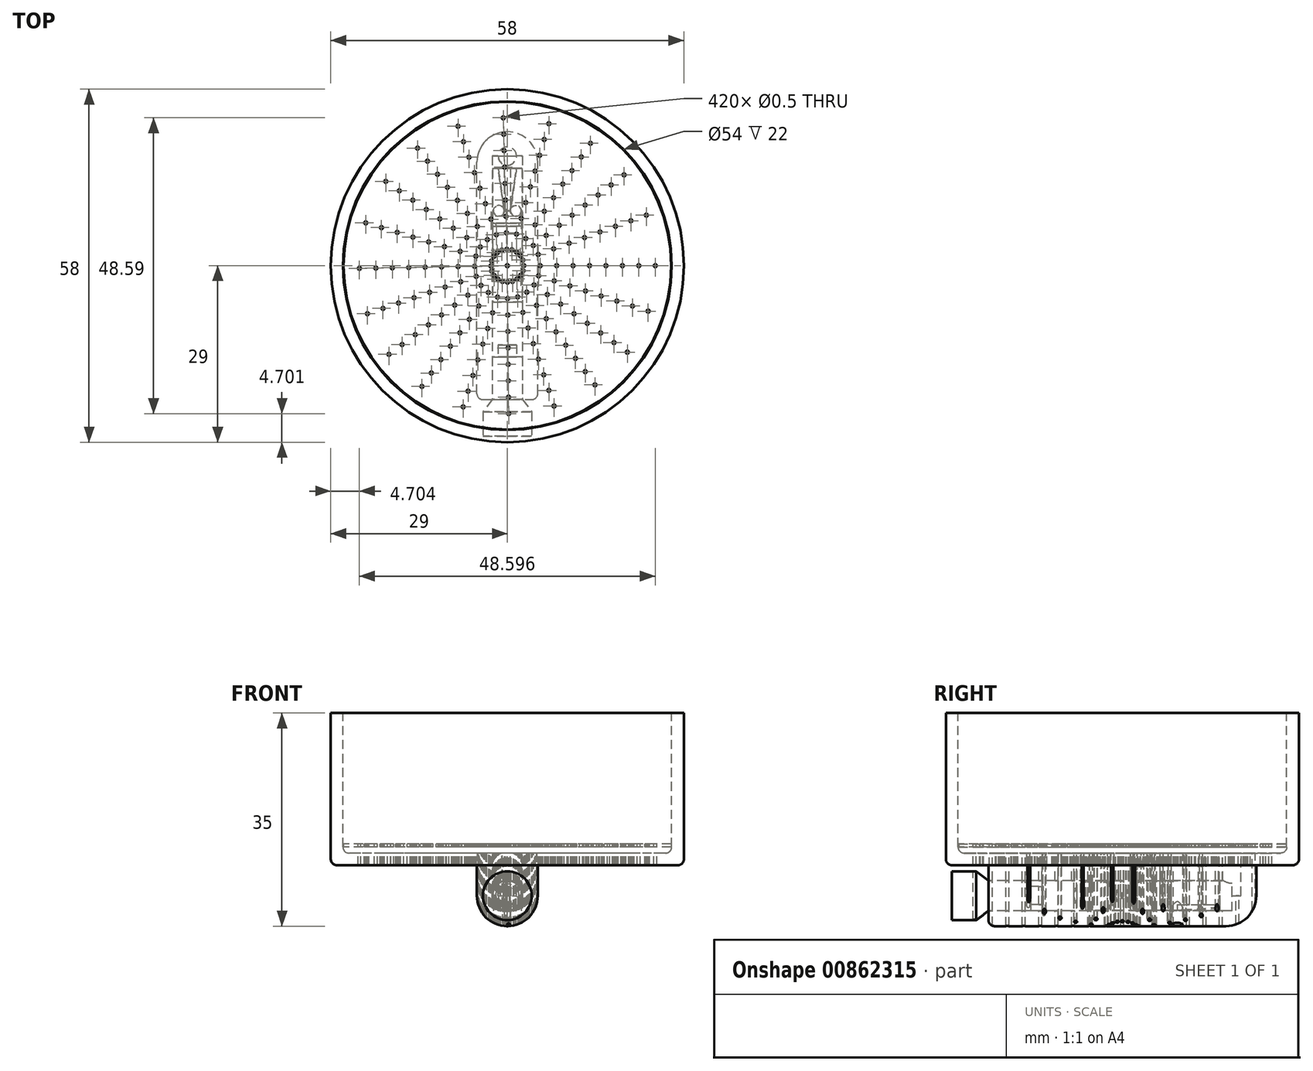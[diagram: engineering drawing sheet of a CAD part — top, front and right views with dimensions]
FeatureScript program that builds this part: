
annotation { "Feature Type Name" : "Feature", "Feature Type Description" : "" }
export const myFeature = defineFeature(function(context is Context, id is Id, definition is map)
    precondition{}
    {
        {
            var Q0;
            Q0=qCreatedBy(makeId("Top.planeOp"),FACE);
            var sketch = newSketch(context, id + "F0", { "sketchPlane" : qUnion([Q0])});
            skCircle(sketch, "E0", {"center": v(0, 0) * mm, "radius": 29 * mm});
            skSolve(sketch);
        }
        {
            var Q0;
            Q0=makeQuery(id+"F0.imprint","IMPRINT",FACE,{"disambiguationData":[TD([[makeQuery(id+"F0.imprint","IMPRINT",EDGE,{"derivedFrom":sQuery(id+"F0.wireOp",EDGE,"E0")}),1.0]])]});
            extrude(context, id + "F1", {"entities" : qUnion([Q0]), "oppositeDirection" : true, "depth" : 25 * mm, "offsetDistance" : 25 * mm});
        }
        {
            var Q0;
            Q0=makeQuery(id+"F1.opExtrude","CAP_FACE",FACE,{"disambiguationData":[OSD([sQuery(id+"F0.wireOp",EDGE,"E0")])],"isStart":true});
            shell(context, id + "F2", {"entities" : qUnion([Q0]), "thickness" : 2 * mm});
        }
        {
            var Q0;
            Q0=qCreatedBy(makeId("Front.planeOp"),FACE);
            var sketch = newSketch(context, id + "F3", { "sketchPlane" : qUnion([Q0])});
            skLineSegment(sketch, "E1.bottom", {"start": v(-5, -25) * mm, "end": v(5, -25) * mm});
            skLineSegment(sketch, "E1.top", {"start": v(-5, -35) * mm, "end": v(5, -35) * mm});
            skLineSegment(sketch, "E1.left", {"start": v(-5, -25) * mm, "end": v(-5, -35) * mm});
            skLineSegment(sketch, "E1.right", {"start": v(5, -25) * mm, "end": v(5, -35) * mm});
            skLineSegment(sketch, "E2.0", {"start": v(-29, -25) * mm, "end": v(29, -25) * mm});
            skSolve(sketch);
        }
        {
            var Q0;
            Q0=makeQuery(id+"F3.imprint","IMPRINT",FACE,{"disambiguationData":[TD([[makeQuery(id+"F3.imprint","IMPRINT",EDGE,{"derivedFrom":sQuery(id+"F3.wireOp",EDGE,"E1.top")}),1.0]])]});
            extrude(context, id + "F4", {"entities" : qUnion([Q0]), "operationType" : NewBodyOperationType.ADD, "depth" : 22 * mm, "offsetDistance" : 25 * mm, "hasSecondDirection" : true, "secondDirectionOppositeDirection" : true, "secondDirectionDepth" : 22 * mm});
        }
        {
            var Q0;
            Q0=makeQuery(id+"F4.opExtrude","CAP_FACE",FACE,{"disambiguationData":[OSD([sQuery(id+"F3.wireOp",EDGE,"E1.top"),sQuery(id+"F3.wireOp",EDGE,"E1.left"),sQuery(id+"F3.wireOp",EDGE,"E1.right"),sQuery(id+"F3.wireOp",EDGE,"E2.0")])],"isStart":false});
            var sketch = newSketch(context, id + "F5", { "sketchPlane" : qUnion([Q0])});
            skCircle(sketch, "E3", {"center": v(0, -30) * mm, "radius": 2.5 * mm});
            skLineSegment(sketch, "E4", {"start": v(-7.7, -30) * mm, "end": v(7.12, -30) * mm, "construction": true});
            skPoint(sketch, "E5", {"position": v(0, -32.45) * mm});
            skSolve(sketch);
        }
        {
            var Q0;
            Q0=makeQuery(id+"F5.imprint","IMPRINT",FACE,{"disambiguationData":[TD([[makeQuery(id+"F5.imprint","IMPRINT",EDGE,{"derivedFrom":sQuery(id+"F5.wireOp",EDGE,"E3")}),1.0]])]});
            extrude(context, id + "F6", {"entities" : qUnion([Q0]), "operationType" : NewBodyOperationType.REMOVE, "oppositeDirection" : true, "depth" : 40 * mm, "offsetDistance" : 25 * mm});
        }
        {
            var Q0;
            Q0=makeQuery(id+"F5.imprint","IMPRINT",FACE,{"disambiguationData":[TD([[makeQuery(id+"F5.imprint","IMPRINT",EDGE,{"derivedFrom":sQuery(id+"F5.wireOp",EDGE,"E3")}),-1.0]])]});
            cPlane(context, id + "F7", {"entities" : qUnion([Q0]), "cplaneType" : CPlaneType.OFFSET, "offset" : 20 * mm, "oppositeDirection" : true, "width" : 150 * mm, "height" : 150 * mm});
        }
        {
            var Q0;
            Q0=qCreatedBy(id+"F7.planeOp",FACE);
            var sketch = newSketch(context, id + "F8", { "sketchPlane" : qUnion([Q0])});
            skCircle(sketch, "E6", {"center": v(0, -30) * mm, "radius": 2.43 * mm});
            skSolve(sketch);
        }
        {
            var Q0;
            Q0=makeQuery(id+"F8.imprint","IMPRINT",FACE,{"disambiguationData":[TD([[makeQuery(id+"F8.imprint","IMPRINT",EDGE,{"derivedFrom":sQuery(id+"F8.wireOp",EDGE,"E6")}),1.0]])]});
            extrude(context, id + "F9", {"entities" : qUnion([Q0]), "oppositeDirection" : true, "depth" : 18 * mm, "offsetDistance" : 25 * mm, "hasSecondDirection" : true, "secondDirectionOppositeDirection" : false, "secondDirectionDepth" : 4 * mm});
        }
        {
            var Q0;
            Q0=sQuery(id+"F5.wireOp",VERTEX,"E5");
            var Q1;
            Q1=qCreatedBy(makeId("Top.planeOp"),FACE);
            cPlane(context, id + "F10", {"entities" : qUnion([Q0, Q1]), "cplaneType" : CPlaneType.PLANE_POINT, "offset" : 25 * mm, "width" : 150 * mm, "height" : 150 * mm});
        }
        {
            var Q0;
            Q0=qCreatedBy(id+"F10.planeOp",FACE);
            var sketch = newSketch(context, id + "F11", { "sketchPlane" : qUnion([Q0])});
            skLineSegment(sketch, "E7", {"start": v(-0.5, 9) * mm, "end": v(0.5, 9) * mm});
            skLineSegment(sketch, "E8", {"start": v(0.5, 9) * mm, "end": v(1.5, 16) * mm});
            skLineSegment(sketch, "E9", {"start": v(-0.5, 9) * mm, "end": v(-1.5, 16) * mm});
            skLineSegment(sketch, "E10", {"start": v(-1.5, 16) * mm, "end": v(1.5, 16) * mm});
            skLineSegment(sketch, "E11", {"start": v(0, -13.78) * mm, "end": v(0, 12.24) * mm, "construction": true});
            skLineSegment(sketch, "E12.0", {"start": v(2.43, 16) * mm, "end": v(-2.43, 16) * mm, "construction": true});
            skSolve(sketch);
        }
        {
            var Q0;
            Q0=makeQuery(id+"F11.imprint","IMPRINT",FACE,{"disambiguationData":[TD([[makeQuery(id+"F11.imprint","IMPRINT",EDGE,{"derivedFrom":sQuery(id+"F11.wireOp",EDGE,"E8")}),1.0]])]});
            extrude(context, id + "F12", {"entities" : qUnion([Q0]), "operationType" : NewBodyOperationType.REMOVE, "depth" : 1 * mm, "offsetDistance" : 25 * mm});
        }
        {
            var Q0;
            Q0=sQuery(id+"F5.wireOp",VERTEX,"E3.center");
            var Q1;
            Q1=qCreatedBy(makeId("Top.planeOp"),FACE);
            cPlane(context, id + "F13", {"entities" : qUnion([Q0, Q1]), "cplaneType" : CPlaneType.PLANE_POINT, "offset" : 25 * mm, "width" : 150 * mm, "height" : 150 * mm});
        }
        {
            var Q0;
            Q0=qCreatedBy(id+"F13.planeOp",FACE);
            var sketch = newSketch(context, id + "F14", { "sketchPlane" : qUnion([Q0])});
            skLineSegment(sketch, "E13.0", {"start": v(2.43, -6) * mm, "end": v(-2.43, -6) * mm, "construction": true});
            skLineSegment(sketch, "E14.bottom", {"start": v(1.92, 6.5) * mm, "end": v(2.42, 6.5) * mm});
            skLineSegment(sketch, "E14.top", {"start": v(1.92, 7) * mm, "end": v(2.42, 7) * mm});
            skLineSegment(sketch, "E14.left", {"start": v(1.92, 6.5) * mm, "end": v(1.92, 7) * mm});
            skLineSegment(sketch, "E14.right", {"start": v(2.42, 6.5) * mm, "end": v(2.42, 7) * mm});
            skLineSegment(sketch, "E15", {"start": v(0, 0) * mm, "end": v(0, -5.82) * mm, "construction": true});
            skPoint(sketch, "E15.endSnap0", {"position": v(0, -6) * mm});
            skSolve(sketch);
        }
        {
            var Q0;
            Q0=makeQuery(id+"F14.imprint","IMPRINT",FACE,{"disambiguationData":[TD([[makeQuery(id+"F14.imprint","IMPRINT",EDGE,{"derivedFrom":sQuery(id+"F14.wireOp",EDGE,"E14.bottom")}),1.0]])]});
            var Q1;
            Q1=sQuery(id+"F14.wireOp",EDGE,"E15");
            revolve(context, id + "F15", {"operationType" : NewBodyOperationType.REMOVE, "surfaceOperationType" : NewSurfaceOperationType.NEW, "entities" : qUnion([Q0]), "axis" : qUnion([Q1]), "revolveType" : RevolveType.FULL, "oppositeDirection" : true});
        }
        {
            var Q0;
            Q0=makeQuery(id+"F4.opExtrude","SWEPT_FACE",FACE,{"disambiguationData":[OSD([sQuery(id+"F3.wireOp",EDGE,"E1.top")])]});
            var sketch = newSketch(context, id + "F16", { "sketchPlane" : qUnion([Q0])});
            skCircle(sketch, "E16", {"center": v(1.4, -9) * mm, "radius": 0.9 * mm});
            skCircle(sketch, "E17", {"center": v(-1.4, -9) * mm, "radius": 0.9 * mm});
            skSolve(sketch);
        }
        {
            var Q0;
            Q0=makeQuery(id+"F16.imprint","IMPRINT",FACE,{"disambiguationData":[TD([[makeQuery(id+"F16.imprint","IMPRINT",EDGE,{"derivedFrom":sQuery(id+"F16.wireOp",EDGE,"E17")}),1.0]])]});
            var Q1;
            Q1=makeQuery(id+"F16.imprint","IMPRINT",FACE,{"disambiguationData":[TD([[makeQuery(id+"F16.imprint","IMPRINT",EDGE,{"derivedFrom":sQuery(id+"F16.wireOp",EDGE,"E16")}),1.0]])]});
            var Q2;
            Q2=makeQuery(id+"F9.opExtrude","SWEPT_BODY",BODY,{"disambiguationData":[OSD([sQuery(id+"F8.wireOp",EDGE,"E6")])]});
            extrude(context, id + "F17", {"entities" : qUnion([Q0, Q1]), "operationType" : NewBodyOperationType.REMOVE, "endBound" : BoundingType.UP_TO_NEXT, "oppositeDirection" : true, "depth" : 25 * mm, "endBoundEntityBody" : qUnion([Q2]), "offsetDistance" : 25 * mm});
        }
        {
            var Q0;
            {var subQ0=sQuery(id+"F0.wireOp",EDGE,"E0");Q0=makeQuery(id+"F2.opShell","OFFSET_FACE",FACE,{"disambiguationData":[OSD([subQ0]),TDD([makeQuery(id+"F1.opExtrude","CAP_FACE",FACE,{"disambiguationData":[OSD([subQ0])],"isStart":false})])]});}
            var sketch = newSketch(context, id + "F18", { "sketchPlane" : qUnion([Q0])});
            skCircle(sketch, "E18", {"center": v(0, 18) * mm, "radius": 1.5 * mm});
            skCircle(sketch, "E19.0.0", {"center": v(0, 0) * mm, "radius": 29 * mm});
            skPoint(sketch, "E20.0", {"position": v(0, 16) * mm});
            skPoint(sketch, "E21", {"position": v(0, 19.5) * mm});
            skSolve(sketch);
        }
        {
            var Q0;
            Q0=makeQuery(id+"F18.imprint","IMPRINT",FACE,{"disambiguationData":[TD([[makeQuery(id+"F18.imprint","IMPRINT",EDGE,{"derivedFrom":sQuery(id+"F18.wireOp",EDGE,"E18")}),1.0]])]});
            var Q1;
            Q1=sQuery(id+"F5.wireOp",VERTEX,"E3.center");
            extrude(context, id + "F19", {"entities" : qUnion([Q0]), "operationType" : NewBodyOperationType.REMOVE, "endBound" : BoundingType.UP_TO_VERTEX, "oppositeDirection" : true, "depth" : 25 * mm, "endBoundEntityVertex" : qUnion([Q1]), "offsetDistance" : 25 * mm});
        }
        {
            var Q0;
            Q0=qCreatedBy(id+"F13.planeOp",FACE);
            var sketch = newSketch(context, id + "F20", { "sketchPlane" : qUnion([Q0])});
            skLineSegment(sketch, "E22.0", {"start": v(2.5, -22) * mm, "end": v(-2.5, -22) * mm, "construction": true});
            skLineSegment(sketch, "E23", {"start": v(2.5, -22) * mm, "end": v(4, -24) * mm});
            skLineSegment(sketch, "E24", {"start": v(0, -27) * mm, "end": v(0, -13) * mm});
            skPoint(sketch, "E24.endSnap0", {"position": v(0, -22) * mm});
            skLineSegment(sketch, "E25", {"start": v(0, -13) * mm, "end": v(1.5, -13) * mm});
            skLineSegment(sketch, "E26", {"start": v(1.5, -13) * mm, "end": v(1.5, -15) * mm});
            skLineSegment(sketch, "E27", {"start": v(1.5, -15) * mm, "end": v(2.5, -15) * mm});
            skLineSegment(sketch, "E28", {"start": v(2.5, -15) * mm, "end": v(2.5, -22) * mm});
            skLineSegment(sketch, "E29", {"start": v(0, -27) * mm, "end": v(0, -28) * mm});
            skLineSegment(sketch, "E30", {"start": v(0, -28) * mm, "end": v(4, -28) * mm});
            skLineSegment(sketch, "E31", {"start": v(4, -28) * mm, "end": v(4, -24) * mm});
            skSolve(sketch);
        }
        {
            var Q0;
            Q0=makeQuery(id+"F20.imprint","IMPRINT",FACE,{"disambiguationData":[TD([[makeQuery(id+"F20.imprint","IMPRINT",EDGE,{"derivedFrom":sQuery(id+"F20.wireOp",EDGE,"E23")}),-1.0]])]});
            var Q1;
            Q1=sQuery(id+"F20.wireOp",EDGE,"E24");
            revolve(context, id + "F21", {"surfaceOperationType" : NewSurfaceOperationType.NEW, "entities" : qUnion([Q0]), "axis" : qUnion([Q1]), "revolveType" : RevolveType.FULL});
        }
        {
            var Q0;
            {var subQ0=sQuery(id+"F0.wireOp",EDGE,"E0");Q0=makeQuery(id+"F2.opShell","OFFSET_FACE",FACE,{"disambiguationData":[OSD([subQ0]),TDD([makeQuery(id+"F1.opExtrude","CAP_FACE",FACE,{"disambiguationData":[OSD([subQ0])],"isStart":false})])]});}
            cPlane(context, id + "F22", {"entities" : qUnion([Q0]), "cplaneType" : CPlaneType.OFFSET, "offset" : 1 * mm, "width" : 150 * mm, "height" : 150 * mm});
        }
        {
            var Q0;
            Q0=qCreatedBy(id+"F22.planeOp",FACE);
            var sketch = newSketch(context, id + "F23", { "sketchPlane" : qUnion([Q0])});
            skCircle(sketch, "E32", {"center": v(0, 0) * mm, "radius": 26.9 * mm});
            skSolve(sketch);
        }
        {
            var Q0;
            Q0=makeQuery(id+"F23.imprint","IMPRINT",FACE,{"disambiguationData":[TD([[makeQuery(id+"F23.imprint","IMPRINT",EDGE,{"derivedFrom":sQuery(id+"F23.wireOp",EDGE,"E32")}),1.0]])]});
            extrude(context, id + "F24", {"entities" : qUnion([Q0]), "depth" : 0.5 * mm, "offsetDistance" : 25 * mm});
        }
        {
            var Q0;
            Q0=makeQuery(id+"F24.opExtrude","CAP_FACE",FACE,{"disambiguationData":[OSD([sQuery(id+"F23.wireOp",EDGE,"E32")])],"isStart":false});
            var sketch = newSketch(context, id + "F25", { "sketchPlane" : qUnion([Q0])});
            skCircle(sketch, "E33", {"center": v(0, 0) * mm, "radius": 0.25 * mm});
            skCircle(sketch, "E34.1.0.0", {"center": v(2.7, 0) * mm, "radius": 0.25 * mm});
            skCircle(sketch, "E34.2.0.0", {"center": v(5.4, 0) * mm, "radius": 0.25 * mm});
            skCircle(sketch, "E34.3.0.0", {"center": v(8.1, 0) * mm, "radius": 0.25 * mm});
            skCircle(sketch, "E34.4.0.0", {"center": v(10.8, 0) * mm, "radius": 0.25 * mm});
            skCircle(sketch, "E34.5.0.0", {"center": v(13.5, 0) * mm, "radius": 0.25 * mm});
            skCircle(sketch, "E34.6.0.0", {"center": v(16.2, 0) * mm, "radius": 0.25 * mm});
            skCircle(sketch, "E34.7.0.0", {"center": v(18.9, 0) * mm, "radius": 0.25 * mm});
            skCircle(sketch, "E34.8.0.0", {"center": v(21.6, 0) * mm, "radius": 0.25 * mm});
            skCircle(sketch, "E34.9.0.0", {"center": v(24.3, 0) * mm, "radius": 0.25 * mm});
            skLineSegment(sketch, "E34.direction1", {"start": v(0, 0) * mm, "end": v(2.7, 0) * mm, "construction": true});
            skLineSegment(sketch, "E35.1.0", {"start": v(0, 0) * mm, "end": v(2.57, -0.83) * mm, "construction": true});
            skCircle(sketch, "E35.1.1", {"center": v(15.42, -4.98) * mm, "radius": 0.25 * mm});
            skCircle(sketch, "E35.1.2", {"center": v(10.28, -3.32) * mm, "radius": 0.25 * mm});
            skCircle(sketch, "E35.1.3", {"center": v(12.85, -4.15) * mm, "radius": 0.25 * mm});
            skCircle(sketch, "E35.1.4", {"center": v(7.7, -2.49) * mm, "radius": 0.25 * mm});
            skCircle(sketch, "E35.1.5", {"center": v(23.12, -7.47) * mm, "radius": 0.25 * mm});
            skCircle(sketch, "E35.1.6", {"center": v(20.56, -6.64) * mm, "radius": 0.25 * mm});
            skCircle(sketch, "E35.1.7", {"center": v(17.99, -5.8) * mm, "radius": 0.25 * mm});
            skCircle(sketch, "E35.1.8", {"center": v(5.14, -1.66) * mm, "radius": 0.25 * mm});
            skCircle(sketch, "E35.1.9", {"center": v(2.57, -0.83) * mm, "radius": 0.25 * mm});
            skLineSegment(sketch, "E35.2.0", {"start": v(0, 0) * mm, "end": v(2.2, -1.58) * mm, "construction": true});
            skCircle(sketch, "E35.2.1", {"center": v(13.14, -9.47) * mm, "radius": 0.25 * mm});
            skCircle(sketch, "E35.2.2", {"center": v(8.76, -6.32) * mm, "radius": 0.25 * mm});
            skCircle(sketch, "E35.2.3", {"center": v(10.95, -7.9) * mm, "radius": 0.25 * mm});
            skCircle(sketch, "E35.2.4", {"center": v(6.57, -4.74) * mm, "radius": 0.25 * mm});
            skCircle(sketch, "E35.2.5", {"center": v(19.71, -14.21) * mm, "radius": 0.25 * mm});
            skCircle(sketch, "E35.2.6", {"center": v(17.52, -12.63) * mm, "radius": 0.25 * mm});
            skCircle(sketch, "E35.2.7", {"center": v(15.33, -11.05) * mm, "radius": 0.25 * mm});
            skCircle(sketch, "E35.2.8", {"center": v(4.38, -3.16) * mm, "radius": 0.25 * mm});
            skCircle(sketch, "E35.2.9", {"center": v(2.2, -1.58) * mm, "radius": 0.25 * mm});
            skLineSegment(sketch, "E35.3.0", {"start": v(0, 0) * mm, "end": v(1.6, -2.18) * mm, "construction": true});
            skCircle(sketch, "E35.3.1", {"center": v(9.6, -13.05) * mm, "radius": 0.25 * mm});
            skCircle(sketch, "E35.3.2", {"center": v(6.4, -8.7) * mm, "radius": 0.25 * mm});
            skCircle(sketch, "E35.3.3", {"center": v(8, -10.88) * mm, "radius": 0.25 * mm});
            skCircle(sketch, "E35.3.4", {"center": v(4.8, -6.53) * mm, "radius": 0.25 * mm});
            skCircle(sketch, "E35.3.5", {"center": v(14.4, -19.58) * mm, "radius": 0.25 * mm});
            skCircle(sketch, "E35.3.6", {"center": v(12.8, -17.4) * mm, "radius": 0.25 * mm});
            skCircle(sketch, "E35.3.7", {"center": v(11.2, -15.23) * mm, "radius": 0.25 * mm});
            skCircle(sketch, "E35.3.8", {"center": v(3.2, -4.35) * mm, "radius": 0.25 * mm});
            skCircle(sketch, "E35.3.9", {"center": v(1.6, -2.18) * mm, "radius": 0.25 * mm});
            skLineSegment(sketch, "E35.4.0", {"start": v(0, 0) * mm, "end": v(0.85, -2.56) * mm, "construction": true});
            skCircle(sketch, "E35.4.1", {"center": v(5.12, -15.37) * mm, "radius": 0.25 * mm});
            skCircle(sketch, "E35.4.2", {"center": v(3.41, -10.25) * mm, "radius": 0.25 * mm});
            skCircle(sketch, "E35.4.3", {"center": v(4.27, -12.8) * mm, "radius": 0.25 * mm});
            skCircle(sketch, "E35.4.4", {"center": v(2.56, -7.68) * mm, "radius": 0.25 * mm});
            skCircle(sketch, "E35.4.5", {"center": v(7.68, -23.05) * mm, "radius": 0.25 * mm});
            skCircle(sketch, "E35.4.6", {"center": v(6.83, -20.5) * mm, "radius": 0.25 * mm});
            skCircle(sketch, "E35.4.7", {"center": v(5.97, -17.93) * mm, "radius": 0.25 * mm});
            skCircle(sketch, "E35.4.8", {"center": v(1.7, -5.12) * mm, "radius": 0.25 * mm});
            skCircle(sketch, "E35.4.9", {"center": v(0.85, -2.56) * mm, "radius": 0.25 * mm});
            skLineSegment(sketch, "E35.5.0", {"start": v(0, 0) * mm, "end": v(0.02, -2.7) * mm, "construction": true});
            skCircle(sketch, "E35.5.1", {"center": v(0.15, -16.2) * mm, "radius": 0.25 * mm});
            skCircle(sketch, "E35.5.2", {"center": v(0.1, -10.8) * mm, "radius": 0.25 * mm});
            skCircle(sketch, "E35.5.3", {"center": v(0.12, -13.5) * mm, "radius": 0.25 * mm});
            skCircle(sketch, "E35.5.4", {"center": v(0.07, -8.1) * mm, "radius": 0.25 * mm});
            skCircle(sketch, "E35.5.5", {"center": v(0.22, -24.3) * mm, "radius": 0.25 * mm});
            skCircle(sketch, "E35.5.6", {"center": v(0.2, -21.6) * mm, "radius": 0.25 * mm});
            skCircle(sketch, "E35.5.7", {"center": v(0.17, -18.9) * mm, "radius": 0.25 * mm});
            skCircle(sketch, "E35.5.8", {"center": v(0.05, -5.4) * mm, "radius": 0.25 * mm});
            skCircle(sketch, "E35.5.9", {"center": v(0.02, -2.7) * mm, "radius": 0.25 * mm});
            skLineSegment(sketch, "E35.6.0", {"start": v(0, 0) * mm, "end": v(-0.8, -2.58) * mm, "construction": true});
            skCircle(sketch, "E35.6.1", {"center": v(-4.84, -15.46) * mm, "radius": 0.25 * mm});
            skCircle(sketch, "E35.6.2", {"center": v(-3.22, -10.3) * mm, "radius": 0.25 * mm});
            skCircle(sketch, "E35.6.3", {"center": v(-4.03, -12.88) * mm, "radius": 0.25 * mm});
            skCircle(sketch, "E35.6.4", {"center": v(-2.42, -7.73) * mm, "radius": 0.25 * mm});
            skCircle(sketch, "E35.6.5", {"center": v(-7.25, -23.2) * mm, "radius": 0.25 * mm});
            skCircle(sketch, "E35.6.6", {"center": v(-6.45, -20.62) * mm, "radius": 0.25 * mm});
            skCircle(sketch, "E35.6.7", {"center": v(-5.64, -18.04) * mm, "radius": 0.25 * mm});
            skCircle(sketch, "E35.6.8", {"center": v(-1.61, -5.15) * mm, "radius": 0.25 * mm});
            skCircle(sketch, "E35.6.9", {"center": v(-0.8, -2.58) * mm, "radius": 0.25 * mm});
            skLineSegment(sketch, "E35.7.0", {"start": v(0, 0) * mm, "end": v(-1.56, -2.2) * mm, "construction": true});
            skCircle(sketch, "E35.7.1", {"center": v(-9.35, -13.23) * mm, "radius": 0.25 * mm});
            skCircle(sketch, "E35.7.2", {"center": v(-6.24, -8.82) * mm, "radius": 0.25 * mm});
            skCircle(sketch, "E35.7.3", {"center": v(-7.8, -11.02) * mm, "radius": 0.25 * mm});
            skCircle(sketch, "E35.7.4", {"center": v(-4.68, -6.61) * mm, "radius": 0.25 * mm});
            skCircle(sketch, "E35.7.5", {"center": v(-14.03, -19.84) * mm, "radius": 0.25 * mm});
            skCircle(sketch, "E35.7.6", {"center": v(-12.47, -17.64) * mm, "radius": 0.25 * mm});
            skCircle(sketch, "E35.7.7", {"center": v(-10.91, -15.43) * mm, "radius": 0.25 * mm});
            skCircle(sketch, "E35.7.8", {"center": v(-3.12, -4.4) * mm, "radius": 0.25 * mm});
            skCircle(sketch, "E35.7.9", {"center": v(-1.56, -2.2) * mm, "radius": 0.25 * mm});
            skLineSegment(sketch, "E35.8.0", {"start": v(0, 0) * mm, "end": v(-2.16, -1.62) * mm, "construction": true});
            skCircle(sketch, "E35.8.1", {"center": v(-12.96, -9.71) * mm, "radius": 0.25 * mm});
            skCircle(sketch, "E35.8.2", {"center": v(-8.64, -6.48) * mm, "radius": 0.25 * mm});
            skCircle(sketch, "E35.8.3", {"center": v(-10.8, -8.1) * mm, "radius": 0.25 * mm});
            skCircle(sketch, "E35.8.4", {"center": v(-6.48, -4.86) * mm, "radius": 0.25 * mm});
            skCircle(sketch, "E35.8.5", {"center": v(-19.45, -14.57) * mm, "radius": 0.25 * mm});
            skCircle(sketch, "E35.8.6", {"center": v(-17.29, -12.95) * mm, "radius": 0.25 * mm});
            skCircle(sketch, "E35.8.7", {"center": v(-15.13, -11.33) * mm, "radius": 0.25 * mm});
            skCircle(sketch, "E35.8.8", {"center": v(-4.32, -3.24) * mm, "radius": 0.25 * mm});
            skCircle(sketch, "E35.8.9", {"center": v(-2.16, -1.62) * mm, "radius": 0.25 * mm});
            skLineSegment(sketch, "E35.9.0", {"start": v(0, 0) * mm, "end": v(-2.55, -0.88) * mm, "construction": true});
            skCircle(sketch, "E35.9.1", {"center": v(-15.32, -5.26) * mm, "radius": 0.25 * mm});
            skCircle(sketch, "E35.9.2", {"center": v(-10.21, -3.5) * mm, "radius": 0.25 * mm});
            skCircle(sketch, "E35.9.3", {"center": v(-12.77, -4.38) * mm, "radius": 0.25 * mm});
            skCircle(sketch, "E35.9.4", {"center": v(-7.66, -2.63) * mm, "radius": 0.25 * mm});
            skCircle(sketch, "E35.9.5", {"center": v(-22.98, -7.9) * mm, "radius": 0.25 * mm});
            skCircle(sketch, "E35.9.6", {"center": v(-20.43, -7.01) * mm, "radius": 0.25 * mm});
            skCircle(sketch, "E35.9.7", {"center": v(-17.88, -6.14) * mm, "radius": 0.25 * mm});
            skCircle(sketch, "E35.9.8", {"center": v(-5.1, -1.75) * mm, "radius": 0.25 * mm});
            skCircle(sketch, "E35.9.9", {"center": v(-2.55, -0.88) * mm, "radius": 0.25 * mm});
            skLineSegment(sketch, "E35.10.0", {"start": v(0, 0) * mm, "end": v(-2.7, -0.05) * mm, "construction": true});
            skCircle(sketch, "E35.10.1", {"center": v(-16.2, -0.3) * mm, "radius": 0.25 * mm});
            skCircle(sketch, "E35.10.2", {"center": v(-10.8, -0.2) * mm, "radius": 0.25 * mm});
            skCircle(sketch, "E35.10.3", {"center": v(-13.5, -0.25) * mm, "radius": 0.25 * mm});
            skCircle(sketch, "E35.10.4", {"center": v(-8.1, -0.15) * mm, "radius": 0.25 * mm});
            skCircle(sketch, "E35.10.5", {"center": v(-24.3, -0.45) * mm, "radius": 0.25 * mm});
            skCircle(sketch, "E35.10.6", {"center": v(-21.6, -0.4) * mm, "radius": 0.25 * mm});
            skCircle(sketch, "E35.10.7", {"center": v(-18.9, -0.35) * mm, "radius": 0.25 * mm});
            skCircle(sketch, "E35.10.8", {"center": v(-5.4, -0.1) * mm, "radius": 0.25 * mm});
            skCircle(sketch, "E35.10.9", {"center": v(-2.7, -0.05) * mm, "radius": 0.25 * mm});
            skLineSegment(sketch, "E35.11.0", {"start": v(0, 0) * mm, "end": v(-2.58, 0.78) * mm, "construction": true});
            skCircle(sketch, "E35.11.1", {"center": v(-15.5, 4.7) * mm, "radius": 0.25 * mm});
            skCircle(sketch, "E35.11.2", {"center": v(-10.34, 3.13) * mm, "radius": 0.25 * mm});
            skCircle(sketch, "E35.11.3", {"center": v(-12.92, 3.91) * mm, "radius": 0.25 * mm});
            skCircle(sketch, "E35.11.4", {"center": v(-7.75, 2.35) * mm, "radius": 0.25 * mm});
            skCircle(sketch, "E35.11.5", {"center": v(-23.26, 7.04) * mm, "radius": 0.25 * mm});
            skCircle(sketch, "E35.11.6", {"center": v(-20.67, 6.26) * mm, "radius": 0.25 * mm});
            skCircle(sketch, "E35.11.7", {"center": v(-18.09, 5.48) * mm, "radius": 0.25 * mm});
            skCircle(sketch, "E35.11.8", {"center": v(-5.17, 1.56) * mm, "radius": 0.25 * mm});
            skCircle(sketch, "E35.11.9", {"center": v(-2.58, 0.78) * mm, "radius": 0.25 * mm});
            skLineSegment(sketch, "E35.12.0", {"start": v(0, 0) * mm, "end": v(-2.22, 1.54) * mm, "construction": true});
            skCircle(sketch, "E35.12.1", {"center": v(-13.31, 9.23) * mm, "radius": 0.25 * mm});
            skCircle(sketch, "E35.12.2", {"center": v(-8.88, 6.15) * mm, "radius": 0.25 * mm});
            skCircle(sketch, "E35.12.3", {"center": v(-11.1, 7.7) * mm, "radius": 0.25 * mm});
            skCircle(sketch, "E35.12.4", {"center": v(-6.66, 4.62) * mm, "radius": 0.25 * mm});
            skCircle(sketch, "E35.12.5", {"center": v(-19.97, 13.85) * mm, "radius": 0.25 * mm});
            skCircle(sketch, "E35.12.6", {"center": v(-17.75, 12.3) * mm, "radius": 0.25 * mm});
            skCircle(sketch, "E35.12.7", {"center": v(-15.53, 10.77) * mm, "radius": 0.25 * mm});
            skCircle(sketch, "E35.12.8", {"center": v(-4.44, 3.08) * mm, "radius": 0.25 * mm});
            skCircle(sketch, "E35.12.9", {"center": v(-2.22, 1.54) * mm, "radius": 0.25 * mm});
            skLineSegment(sketch, "E35.13.0", {"start": v(0, 0) * mm, "end": v(-1.64, 2.15) * mm, "construction": true});
            skCircle(sketch, "E35.13.1", {"center": v(-9.83, 12.87) * mm, "radius": 0.25 * mm});
            skCircle(sketch, "E35.13.2", {"center": v(-6.55, 8.58) * mm, "radius": 0.25 * mm});
            skCircle(sketch, "E35.13.3", {"center": v(-8.2, 10.73) * mm, "radius": 0.25 * mm});
            skCircle(sketch, "E35.13.4", {"center": v(-4.92, 6.44) * mm, "radius": 0.25 * mm});
            skCircle(sketch, "E35.13.5", {"center": v(-14.75, 19.31) * mm, "radius": 0.25 * mm});
            skCircle(sketch, "E35.13.6", {"center": v(-13.1, 17.17) * mm, "radius": 0.25 * mm});
            skCircle(sketch, "E35.13.7", {"center": v(-11.47, 15.02) * mm, "radius": 0.25 * mm});
            skCircle(sketch, "E35.13.8", {"center": v(-3.28, 4.3) * mm, "radius": 0.25 * mm});
            skCircle(sketch, "E35.13.9", {"center": v(-1.64, 2.15) * mm, "radius": 0.25 * mm});
            skLineSegment(sketch, "E35.14.0", {"start": v(0, 0) * mm, "end": v(-0.9, 2.55) * mm, "construction": true});
            skCircle(sketch, "E35.14.1", {"center": v(-5.4, 15.27) * mm, "radius": 0.25 * mm});
            skCircle(sketch, "E35.14.2", {"center": v(-3.6, 10.18) * mm, "radius": 0.25 * mm});
            skCircle(sketch, "E35.14.3", {"center": v(-4.5, 12.73) * mm, "radius": 0.25 * mm});
            skCircle(sketch, "E35.14.4", {"center": v(-2.7, 7.64) * mm, "radius": 0.25 * mm});
            skCircle(sketch, "E35.14.5", {"center": v(-8.1, 22.9) * mm, "radius": 0.25 * mm});
            skCircle(sketch, "E35.14.6", {"center": v(-7.2, 20.36) * mm, "radius": 0.25 * mm});
            skCircle(sketch, "E35.14.7", {"center": v(-6.3, 17.82) * mm, "radius": 0.25 * mm});
            skCircle(sketch, "E35.14.8", {"center": v(-1.8, 5.1) * mm, "radius": 0.25 * mm});
            skCircle(sketch, "E35.14.9", {"center": v(-0.9, 2.55) * mm, "radius": 0.25 * mm});
            skLineSegment(sketch, "E35.15.0", {"start": v(0, 0) * mm, "end": v(-0.07, 2.7) * mm, "construction": true});
            skCircle(sketch, "E35.15.1", {"center": v(-0.45, 16.2) * mm, "radius": 0.25 * mm});
            skCircle(sketch, "E35.15.2", {"center": v(-0.3, 10.8) * mm, "radius": 0.25 * mm});
            skCircle(sketch, "E35.15.3", {"center": v(-0.37, 13.5) * mm, "radius": 0.25 * mm});
            skCircle(sketch, "E35.15.4", {"center": v(-0.22, 8.1) * mm, "radius": 0.25 * mm});
            skCircle(sketch, "E35.15.5", {"center": v(-0.67, 24.3) * mm, "radius": 0.25 * mm});
            skCircle(sketch, "E35.15.6", {"center": v(-0.6, 21.6) * mm, "radius": 0.25 * mm});
            skCircle(sketch, "E35.15.7", {"center": v(-0.52, 18.9) * mm, "radius": 0.25 * mm});
            skCircle(sketch, "E35.15.8", {"center": v(-0.15, 5.4) * mm, "radius": 0.25 * mm});
            skCircle(sketch, "E35.15.9", {"center": v(-0.07, 2.7) * mm, "radius": 0.25 * mm});
            skLineSegment(sketch, "E35.16.0", {"start": v(0, 0) * mm, "end": v(0.76, 2.6) * mm, "construction": true});
            skCircle(sketch, "E35.16.1", {"center": v(4.55, 15.55) * mm, "radius": 0.25 * mm});
            skCircle(sketch, "E35.16.2", {"center": v(3.03, 10.37) * mm, "radius": 0.25 * mm});
            skCircle(sketch, "E35.16.3", {"center": v(3.8, 12.96) * mm, "radius": 0.25 * mm});
            skCircle(sketch, "E35.16.4", {"center": v(2.28, 7.77) * mm, "radius": 0.25 * mm});
            skCircle(sketch, "E35.16.5", {"center": v(6.83, 23.32) * mm, "radius": 0.25 * mm});
            skCircle(sketch, "E35.16.6", {"center": v(6.07, 20.73) * mm, "radius": 0.25 * mm});
            skCircle(sketch, "E35.16.7", {"center": v(5.3, 18.14) * mm, "radius": 0.25 * mm});
            skCircle(sketch, "E35.16.8", {"center": v(1.52, 5.18) * mm, "radius": 0.25 * mm});
            skCircle(sketch, "E35.16.9", {"center": v(0.76, 2.6) * mm, "radius": 0.25 * mm});
            skLineSegment(sketch, "E35.17.0", {"start": v(0, 0) * mm, "end": v(1.52, 2.23) * mm, "construction": true});
            skCircle(sketch, "E35.17.1", {"center": v(9.1, 13.4) * mm, "radius": 0.25 * mm});
            skCircle(sketch, "E35.17.2", {"center": v(6.07, 8.93) * mm, "radius": 0.25 * mm});
            skCircle(sketch, "E35.17.3", {"center": v(7.6, 11.16) * mm, "radius": 0.25 * mm});
            skCircle(sketch, "E35.17.4", {"center": v(4.55, 6.7) * mm, "radius": 0.25 * mm});
            skCircle(sketch, "E35.17.5", {"center": v(13.66, 20.1) * mm, "radius": 0.25 * mm});
            skCircle(sketch, "E35.17.6", {"center": v(12.14, 17.86) * mm, "radius": 0.25 * mm});
            skCircle(sketch, "E35.17.7", {"center": v(10.63, 15.63) * mm, "radius": 0.25 * mm});
            skCircle(sketch, "E35.17.8", {"center": v(3.04, 4.47) * mm, "radius": 0.25 * mm});
            skCircle(sketch, "E35.17.9", {"center": v(1.52, 2.23) * mm, "radius": 0.25 * mm});
            skLineSegment(sketch, "E35.18.0", {"start": v(0, 0) * mm, "end": v(2.13, 1.66) * mm, "construction": true});
            skCircle(sketch, "E35.18.1", {"center": v(12.78, 9.95) * mm, "radius": 0.25 * mm});
            skCircle(sketch, "E35.18.2", {"center": v(8.52, 6.63) * mm, "radius": 0.25 * mm});
            skCircle(sketch, "E35.18.3", {"center": v(10.65, 8.3) * mm, "radius": 0.25 * mm});
            skCircle(sketch, "E35.18.4", {"center": v(6.4, 4.98) * mm, "radius": 0.25 * mm});
            skCircle(sketch, "E35.18.5", {"center": v(19.18, 14.93) * mm, "radius": 0.25 * mm});
            skCircle(sketch, "E35.18.6", {"center": v(17.05, 13.27) * mm, "radius": 0.25 * mm});
            skCircle(sketch, "E35.18.7", {"center": v(14.91, 11.6) * mm, "radius": 0.25 * mm});
            skCircle(sketch, "E35.18.8", {"center": v(4.26, 3.32) * mm, "radius": 0.25 * mm});
            skCircle(sketch, "E35.18.9", {"center": v(2.13, 1.66) * mm, "radius": 0.25 * mm});
            skLineSegment(sketch, "E35.19.0", {"start": v(0, 0) * mm, "end": v(2.54, 0.92) * mm, "construction": true});
            skCircle(sketch, "E35.19.1", {"center": v(15.22, 5.54) * mm, "radius": 0.25 * mm});
            skCircle(sketch, "E35.19.2", {"center": v(10.15, 3.7) * mm, "radius": 0.25 * mm});
            skCircle(sketch, "E35.19.3", {"center": v(12.69, 4.62) * mm, "radius": 0.25 * mm});
            skCircle(sketch, "E35.19.4", {"center": v(7.61, 2.77) * mm, "radius": 0.25 * mm});
            skCircle(sketch, "E35.19.5", {"center": v(22.83, 8.31) * mm, "radius": 0.25 * mm});
            skCircle(sketch, "E35.19.6", {"center": v(20.3, 7.39) * mm, "radius": 0.25 * mm});
            skCircle(sketch, "E35.19.7", {"center": v(17.76, 6.46) * mm, "radius": 0.25 * mm});
            skCircle(sketch, "E35.19.8", {"center": v(5.07, 1.85) * mm, "radius": 0.25 * mm});
            skCircle(sketch, "E35.19.9", {"center": v(2.54, 0.92) * mm, "radius": 0.25 * mm});
            skLineSegment(sketch, "E35.anchor2", {"start": v(0, 0) * mm, "end": v(2.54, 0.92) * mm, "construction": true});
            skSolve(sketch);
        }
        {
            var Q0;
            Q0=qSketchRegion(id+"F25",true);
            extrude(context, id + "F26", {"entities" : qUnion([Q0]), "operationType" : NewBodyOperationType.REMOVE, "endBound" : BoundingType.THROUGH_ALL, "oppositeDirection" : true, "depth" : 25 * mm, "offsetDistance" : 25 * mm});
        }
        {
            var Q0;
            {var subQ0=sQuery(id+"F0.wireOp",EDGE,"E0");Q0=makeQuery(id+"F2.opShell","OFFSET_EDGE",EDGE,{"disambiguationData":[OSD([subQ0]),TDD([makeQuery(id+"F1.opExtrude","CAP_EDGE",EDGE,{"disambiguationData":[OSD([subQ0])],"isStart":false})])]});}
            fillet(context, id + "F27", {"entities" : qUnion([Q0]), "radius" : 1 * mm, "tangentPropagation" : true, "allowEdgeOverflow" : false});
        }
        {
            var Q0;
            Q0=makeQuery(id+"F4.opExtrude","SWEPT_EDGE",EDGE,{"disambiguationData":[OSD([sQuery(id+"F3.wireOp",EDGE,"E1.right"),sQuery(id+"F3.wireOp",EDGE,"E2.0")])]});
            var Q1;
            Q1=makeQuery(id+"F4.opExtrude","SWEPT_EDGE",EDGE,{"disambiguationData":[OSD([sQuery(id+"F3.wireOp",EDGE,"E1.top"),sQuery(id+"F3.wireOp",EDGE,"E1.right")])]});
            var Q2;
            Q2=makeQuery(id+"F4.opExtrude","SWEPT_EDGE",EDGE,{"disambiguationData":[OSD([sQuery(id+"F3.wireOp",EDGE,"E1.top"),sQuery(id+"F3.wireOp",EDGE,"E1.left")])]});
            var Q3;
            Q3=makeQuery(id+"F4.opExtrude","SWEPT_EDGE",EDGE,{"disambiguationData":[OSD([sQuery(id+"F3.wireOp",EDGE,"E1.left"),sQuery(id+"F3.wireOp",EDGE,"E2.0")])]});
            fillet(context, id + "F28", {"entities" : qUnion([Q0, Q1, Q2, Q3]), "radius" : 5 * mm, "tangentPropagation" : true, "allowEdgeOverflow" : false});
        }
        {
            var Q0;
            {var subQ0=sQuery(id+"F3.wireOp",EDGE,"E1.left");var subQ1=sQuery(id+"F3.wireOp",EDGE,"E1.top");Q0=makeQuery(id+"F28.opFillet","BLEND_EDGE",EDGE,{"blendedFrom":[makeQuery(id+"F4.opExtrude","SWEPT_EDGE",EDGE,{"disambiguationData":[OSD([subQ1,subQ0])]}),makeQuery(id+"F4.opExtrude","CAP_FACE",FACE,{"disambiguationData":[OSD([subQ1,subQ0,sQuery(id+"F3.wireOp",EDGE,"E1.right"),sQuery(id+"F3.wireOp",EDGE,"E2.0")])],"isStart":true})],"blendedInto":[makeQuery(id+"F4.opExtrude","CAP_FACE",FACE,{"disambiguationData":[OSD([subQ1,subQ0,sQuery(id+"F3.wireOp",EDGE,"E1.right"),sQuery(id+"F3.wireOp",EDGE,"E2.0")])],"isStart":true})]});}
            fillet(context, id + "F29", {"entities" : qUnion([Q0]), "radius" : 5 * mm, "tangentPropagation" : true, "allowEdgeOverflow" : false});
        }
        {
            var Q0;
            {var subQ0=sQuery(id+"F3.wireOp",EDGE,"E1.left");var subQ1=sQuery(id+"F3.wireOp",EDGE,"E1.top");Q0=makeQuery(id+"F28.opFillet","BLEND_EDGE",EDGE,{"blendedFrom":[makeQuery(id+"F4.opExtrude","SWEPT_EDGE",EDGE,{"disambiguationData":[OSD([subQ1,subQ0])]}),makeQuery(id+"F4.opExtrude","CAP_FACE",FACE,{"disambiguationData":[OSD([subQ1,subQ0,sQuery(id+"F3.wireOp",EDGE,"E1.right"),sQuery(id+"F3.wireOp",EDGE,"E2.0")])],"isStart":false})],"blendedInto":[makeQuery(id+"F4.opExtrude","CAP_FACE",FACE,{"disambiguationData":[OSD([subQ1,subQ0,sQuery(id+"F3.wireOp",EDGE,"E1.right"),sQuery(id+"F3.wireOp",EDGE,"E2.0")])],"isStart":false})]});}
            fillet(context, id + "F30", {"entities" : qUnion([Q0]), "radius" : 1 * mm, "tangentPropagation" : true, "allowEdgeOverflow" : false});
        }
        {
            var Q0;
            Q0=makeQuery(id+"F1.opExtrude","CAP_EDGE",EDGE,{"disambiguationData":[OSD([sQuery(id+"F0.wireOp",EDGE,"E0")])],"isStart":false});
            fillet(context, id + "F31", {"entities" : qUnion([Q0]), "radius" : 1 * mm, "tangentPropagation" : true, "allowEdgeOverflow" : false});
        }
    });
